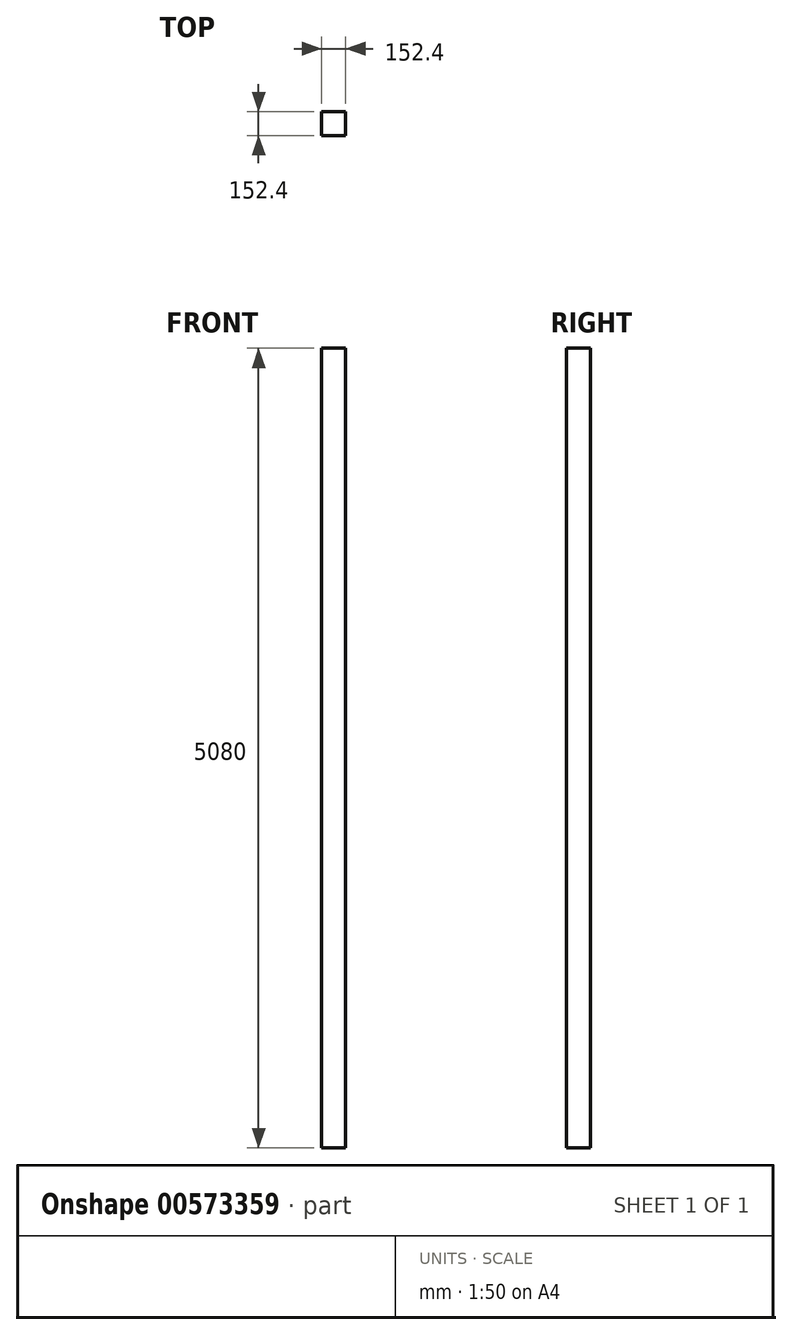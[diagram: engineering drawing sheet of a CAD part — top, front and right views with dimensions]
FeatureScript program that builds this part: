
annotation { "Feature Type Name" : "Feature", "Feature Type Description" : "" }
export const myFeature = defineFeature(function(context is Context, id is Id, definition is map)
    precondition{}
    {
        {
            var Q0;
            Q0=qCreatedBy(makeId("Top.planeOp"),FACE);
            var sketch = newSketch(context, id + "F0", { "sketchPlane" : qUnion([Q0])});
            skLineSegment(sketch, "E0.bottom", {"start": v(76.2, -76.2) * mm, "end": v(-76.2, -76.2) * mm});
            skLineSegment(sketch, "E0.top", {"start": v(76.2, 76.2) * mm, "end": v(-76.2, 76.2) * mm});
            skLineSegment(sketch, "E0.left", {"start": v(76.2, -76.2) * mm, "end": v(76.2, 76.2) * mm});
            skLineSegment(sketch, "E0.right", {"start": v(-76.2, -76.2) * mm, "end": v(-76.2, 76.2) * mm});
            skPoint(sketch, "E0.middle", {"position": v(0, 0) * mm});
            skSolve(sketch);
        }
        {
            var Q0;
            Q0=makeQuery(id+"F0.imprint","IMPRINT",FACE,{"disambiguationData":[TD([[makeQuery(id+"F0.imprint","IMPRINT",EDGE,{"derivedFrom":sQuery(id+"F0.wireOp",EDGE,"E0.bottom")}),-1.0]])]});
            extrude(context, id + "F1", {"entities" : qUnion([Q0]), "depth" : 5080 * mm, "offsetDistance" : 25.4 * mm});
        }
    });
